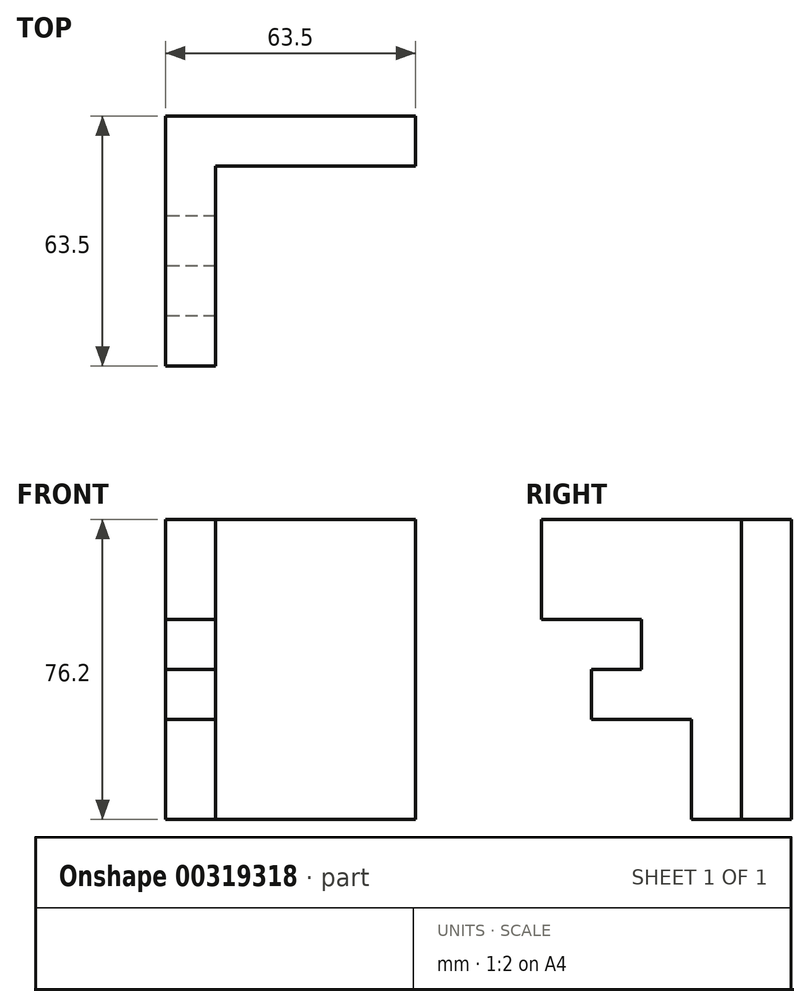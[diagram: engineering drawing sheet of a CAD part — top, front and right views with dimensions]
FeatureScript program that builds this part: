
annotation { "Feature Type Name" : "Feature", "Feature Type Description" : "" }
export const myFeature = defineFeature(function(context is Context, id is Id, definition is map)
    precondition{}
    {
        {
            var Q0;
            Q0=qCreatedBy(makeId("Right.planeOp"),FACE);
            var sketch = newSketch(context, id + "F0", { "sketchPlane" : qUnion([Q0])});
            skLineSegment(sketch, "E0", {"start": v(-13.97, -63.9) * mm, "end": v(-39.37, -63.9) * mm});
            skLineSegment(sketch, "E1", {"start": v(-39.37, -63.9) * mm, "end": v(-39.37, -38.5) * mm});
            skLineSegment(sketch, "E2", {"start": v(-39.37, -38.5) * mm, "end": v(-64.77, -38.5) * mm});
            skLineSegment(sketch, "E3", {"start": v(-64.77, -38.5) * mm, "end": v(-64.77, -25.8) * mm});
            skLineSegment(sketch, "E4", {"start": v(-77.47, -13.1) * mm, "end": v(-77.47, 12.3) * mm});
            skLineSegment(sketch, "E5", {"start": v(-77.47, 12.3) * mm, "end": v(-13.97, 12.3) * mm});
            skLineSegment(sketch, "E6", {"start": v(-13.97, 12.3) * mm, "end": v(-13.97, -63.9) * mm});
            skLineSegment(sketch, "E7", {"start": v(-64.77, -25.8) * mm, "end": v(-52.07, -25.8) * mm});
            skLineSegment(sketch, "E8", {"start": v(-52.07, -25.8) * mm, "end": v(-52.07, -13.1) * mm});
            skLineSegment(sketch, "E9", {"start": v(-52.07, -13.1) * mm, "end": v(-77.47, -13.1) * mm});
            skSolve(sketch);
        }
        {
            var Q0;
            Q0=makeQuery(id+"F0.imprint","IMPRINT",FACE,{"disambiguationData":[TD([[makeQuery(id+"F0.imprint","IMPRINT",EDGE,{"derivedFrom":sQuery(id+"F0.wireOp",EDGE,"E0")}),-1.0]])]});
            extrude(context, id + "F1", {"entities" : qUnion([Q0]), "depth" : 12.7 * mm});
        }
        {
            var Q0;
            Q0=makeQuery(id+"F1.opExtrude","CAP_FACE",FACE,{"disambiguationData":[OSD([sQuery(id+"F0.wireOp",EDGE,"E0"),sQuery(id+"F0.wireOp",EDGE,"E1"),sQuery(id+"F0.wireOp",EDGE,"E2"),sQuery(id+"F0.wireOp",EDGE,"E3"),sQuery(id+"F0.wireOp",EDGE,"E4"),sQuery(id+"F0.wireOp",EDGE,"E5"),sQuery(id+"F0.wireOp",EDGE,"E6"),sQuery(id+"F0.wireOp",EDGE,"E7"),sQuery(id+"F0.wireOp",EDGE,"E8"),sQuery(id+"F0.wireOp",EDGE,"E9")])],"isStart":false});
            var sketch = newSketch(context, id + "F2", { "sketchPlane" : qUnion([Q0])});
            skLineSegment(sketch, "E10", {"start": v(-13.97, 12.3) * mm, "end": v(-26.67, 12.3) * mm});
            skLineSegment(sketch, "E11", {"start": v(-26.67, 12.3) * mm, "end": v(-26.67, -63.9) * mm});
            skLineSegment(sketch, "E12", {"start": v(-26.67, -63.9) * mm, "end": v(-13.97, -63.9) * mm});
            skLineSegment(sketch, "E13", {"start": v(-13.97, -63.9) * mm, "end": v(-13.97, 12.3) * mm});
            skSolve(sketch);
        }
        {
            var Q0;
            Q0=makeQuery(id+"F2.imprint","IMPRINT",FACE,{"disambiguationData":[TD([[makeQuery(id+"F2.imprint","IMPRINT",EDGE,{"derivedFrom":sQuery(id+"F2.wireOp",EDGE,"E10")}),-1.0]])]});
            extrude(context, id + "F3", {"entities" : qUnion([Q0]), "operationType" : NewBodyOperationType.ADD, "depth" : 50.8 * mm});
        }
    });
